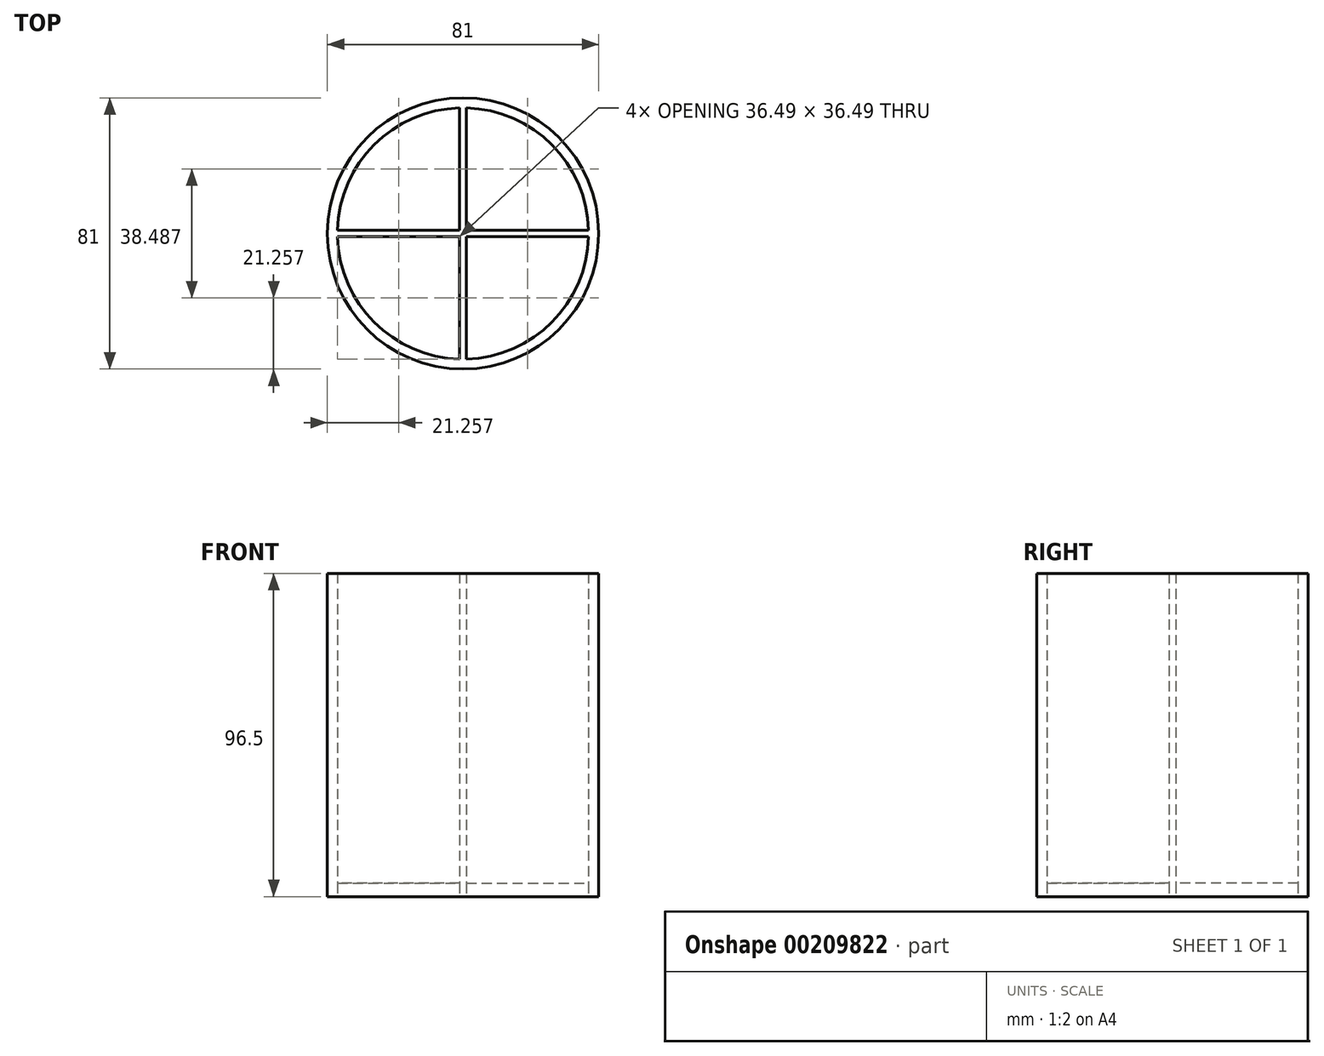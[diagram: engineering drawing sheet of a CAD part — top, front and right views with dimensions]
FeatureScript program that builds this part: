
annotation { "Feature Type Name" : "Feature", "Feature Type Description" : "" }
export const myFeature = defineFeature(function(context is Context, id is Id, definition is map)
    precondition{}
    {
        {
            var Q0;
            Q0=qCreatedBy(makeId("Top.planeOp"),FACE);
            var sketch = newSketch(context, id + "F0", { "sketchPlane" : qUnion([Q0])});
            skArc(sketch, "E0", {"start": v(-37.49, -1) * mm, "mid": v(-26.52, -26.52) * mm, "end": v(-1, -37.49) * mm});
            skCircle(sketch, "E1.0", {"center": v(0, 0) * mm, "radius": 40.5 * mm});
            skLineSegment(sketch, "E2.0", {"start": v(-37.5, -1) * mm, "end": v(-1, -1) * mm});
            skLineSegment(sketch, "E3.0", {"start": v(-37.5, 1) * mm, "end": v(-1, 1) * mm});
            skLineSegment(sketch, "E4.0", {"start": v(-1, 37.5) * mm, "end": v(-1, 1) * mm});
            skLineSegment(sketch, "E5.0", {"start": v(1, 37.5) * mm, "end": v(1, 1) * mm});
            skLineSegment(sketch, "E6.0", {"start": v(-1, -1) * mm, "end": v(-1, -37.5) * mm});
            skLineSegment(sketch, "E7.0", {"start": v(1, -1) * mm, "end": v(1, -37.5) * mm});
            skPoint(sketch, "E8.orphan", {"position": v(0, 37.5) * mm});
            skArc(sketch, "E9.trimOffspring", {"start": v(1, -37.49) * mm, "mid": v(26.52, -26.52) * mm, "end": v(37.49, -1) * mm});
            skArc(sketch, "E10.trimOffspring", {"start": v(37.49, 1) * mm, "mid": v(26.52, 26.52) * mm, "end": v(1, 37.49) * mm});
            skArc(sketch, "E11.trimOffspring", {"start": v(-1, 37.49) * mm, "mid": v(-26.52, 26.52) * mm, "end": v(-37.49, 1) * mm});
            skLineSegment(sketch, "E12.trimOffspring", {"start": v(1, -1) * mm, "end": v(37.5, -1) * mm});
            skLineSegment(sketch, "E13.trimOffspring", {"start": v(1, 1) * mm, "end": v(37.5, 1) * mm});
            skSolve(sketch);
        }
        {
            var Q0;
            {var subQ0=sQuery(id+"F0.wireOp",EDGE,"E0");Q0=makeQuery(id+"F0.imprint","IMPRINT",FACE,{"disambiguationData":[TD([[makeQuery(id+"F0.imprint","IMPRINT",EDGE,{"derivedFrom":subQ0}),1.0]])]});}
            var Q1;
            {var subQ3=sQuery(id+"F0.wireOp",EDGE,"E11.trimOffspring");Q1=makeQuery(id+"F0.imprint","IMPRINT",FACE,{"disambiguationData":[TD([[makeQuery(id+"F0.imprint","IMPRINT",EDGE,{"derivedFrom":subQ3}),1.0]])]});}
            var Q2;
            {var subQ3=sQuery(id+"F0.wireOp",EDGE,"E10.trimOffspring");Q2=makeQuery(id+"F0.imprint","IMPRINT",FACE,{"disambiguationData":[TD([[makeQuery(id+"F0.imprint","IMPRINT",EDGE,{"derivedFrom":subQ3}),1.0]])]});}
            var Q3;
            {var subQ3=sQuery(id+"F0.wireOp",EDGE,"E9.trimOffspring");Q3=makeQuery(id+"F0.imprint","IMPRINT",FACE,{"disambiguationData":[TD([[makeQuery(id+"F0.imprint","IMPRINT",EDGE,{"derivedFrom":subQ3}),1.0]])]});}
            extrude(context, id + "F1", {"entities" : qUnion([Q0, Q1, Q2, Q3]), "depth" : 4 * mm});
        }
        {
            var Q0;
            {var subQ4=sQuery(id+"F0.wireOp",EDGE,"E0");Q0=makeQuery(id+"F0.imprint","IMPRINT",FACE,{"disambiguationData":[TD([[makeQuery(id+"F0.imprint","IMPRINT",EDGE,{"derivedFrom":subQ4}),-1.0]])]});}
            extrude(context, id + "F2", {"entities" : qUnion([Q0]), "depth" : 96.5 * mm});
        }
    });
